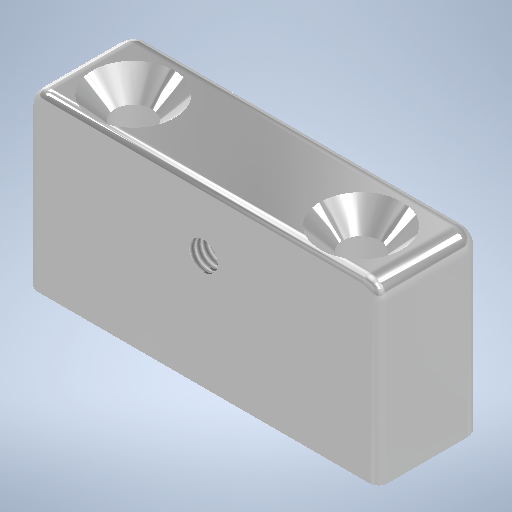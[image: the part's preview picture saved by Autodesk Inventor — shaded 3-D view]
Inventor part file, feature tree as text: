
AUTODESK INVENTOR PART (.ipt)
format: ipt  version: 2025 (Build 290162010, 162A)  size: 291,328 bytes
history: native  units: mm
features: sketch x3, hole x2, fillet x2, extrude x1
ambient origin geometry x8: Origin, YZ Plane, XZ Plane, XY Plane, X Axis, Y Axis, Z Axis, Center Point
bodies: Volumenkörper1 (feature_tree)
feature tree (8):
  extrude  "Extrusion1"  Depth=12.0mm
  hole  "Bohrung1"  [1 undecoded]
  hole  "Bohrung4"  [1 undecoded]
  fillet  "Rundung2"  Radius=7.0mm
  fillet  "Rundung3"  Radius=2.0mm
  sketch  "Skizze1"  dims[d0=40.0mm d1=12.0mm]
  sketch  "Skizze2"  dims[d2=20.0mm d3=0.0mm d4=7.0mm]
  sketch  "Skizze3"  dims[d5=4.3mm d6=6.0mm d7=9.4mm d8=4.0mm d9=90.0deg d10=15.0mm d11=20.594885mm d12=7.0mm d14=7.0mm d29=3.242mm d30=8.0mm d31=4.0mm d32=2.0mm d33=90.0deg d34=10.0mm d35=20.594885mm d36=2.0mm d37=1.0mm d38=0.0625mm d39=0.75mm d40=0.375mm]
note: 2 required parameter values undecoded (feature->parameter linkage not recoverable at this tier; creation-order binding heuristic only, values carry confidence <= 0.55)
